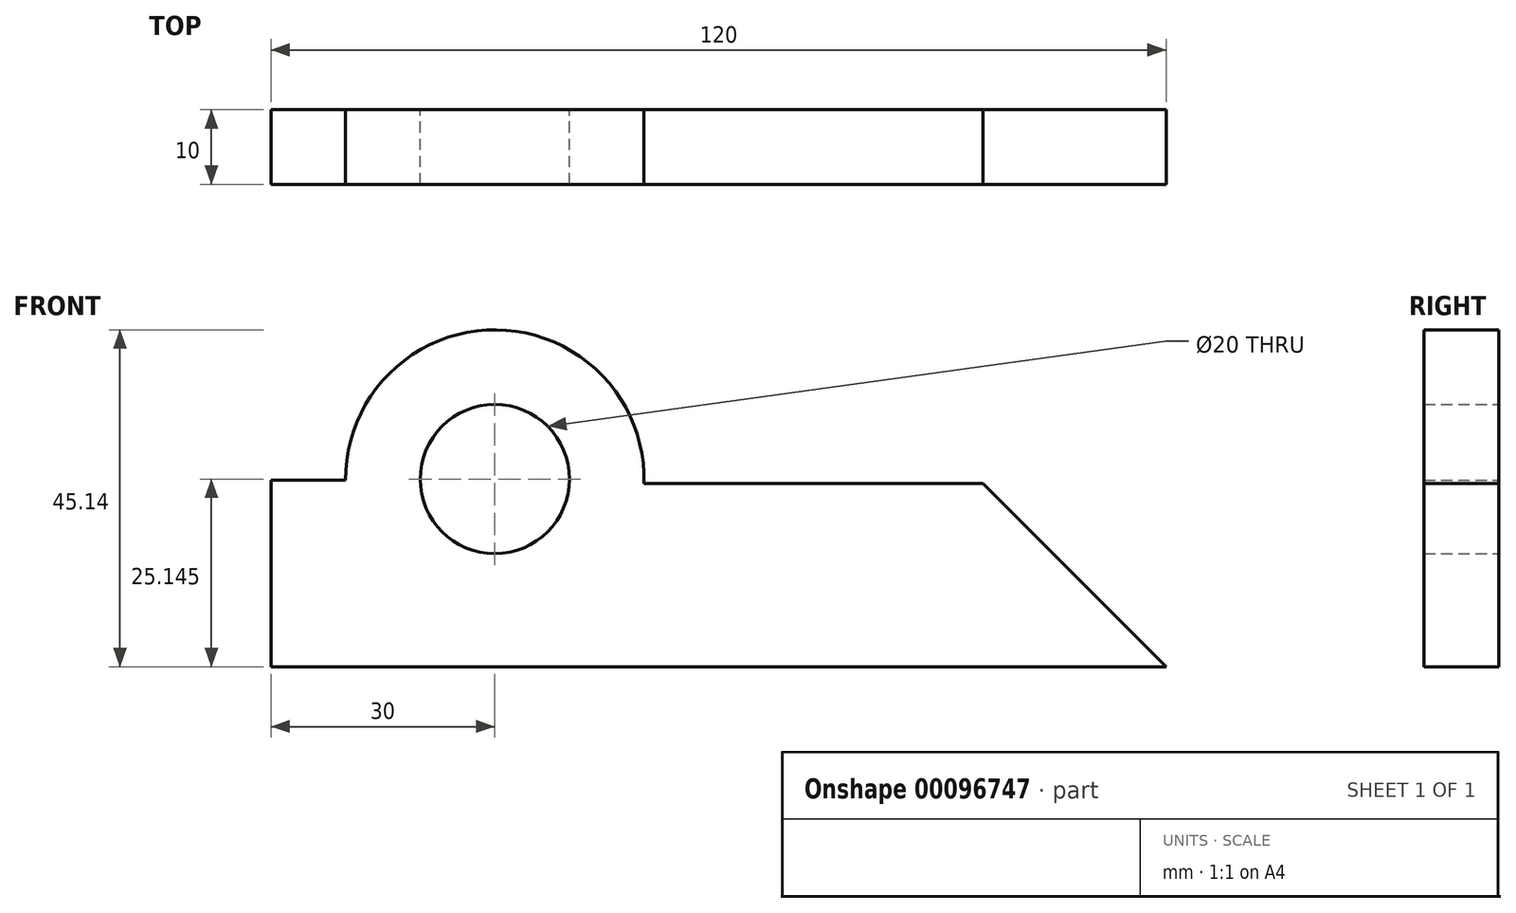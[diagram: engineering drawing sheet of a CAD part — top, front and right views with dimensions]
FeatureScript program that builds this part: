
annotation { "Feature Type Name" : "Feature", "Feature Type Description" : "" }
export const myFeature = defineFeature(function(context is Context, id is Id, definition is map)
    precondition{}
    {
        {
            var Q0;
            Q0=qCreatedBy(makeId("Front.planeOp"),FACE);
            var sketch = newSketch(context, id + "F0", { "sketchPlane" : qUnion([Q0])});
            skLineSegment(sketch, "E0", {"start": v(0, 0) * mm, "end": v(0, 25) * mm});
            skLineSegment(sketch, "E1", {"start": v(0, 25) * mm, "end": v(10, 25) * mm});
            skLineSegment(sketch, "E2", {"start": v(0, 0) * mm, "end": v(120, 0) * mm});
            skLineSegment(sketch, "E3", {"start": v(120, 0) * mm, "end": v(95.43, 24.57) * mm});
            skLineSegment(sketch, "E4", {"start": v(95.43, 24.57) * mm, "end": v(50, 24.57) * mm});
            skCircle(sketch, "E5", {"center": v(30, 25.14) * mm, "radius": 10 * mm});
            skArc(sketch, "E6", {"start": v(50, 24.57) * mm, "mid": v(30.22, 45.14) * mm, "end": v(10, 25) * mm});
            skSolve(sketch);
        }
        {
            var Q0;
            Q0=makeQuery(id+"F0.imprint","IMPRINT",FACE,{"disambiguationData":[TD([[makeQuery(id+"F0.imprint","IMPRINT",EDGE,{"derivedFrom":sQuery(id+"F0.wireOp",EDGE,"E0")}),-1.0]])]});
            extrude(context, id + "F1", {"entities" : qUnion([Q0]), "depth" : 10 * mm});
        }
    });
